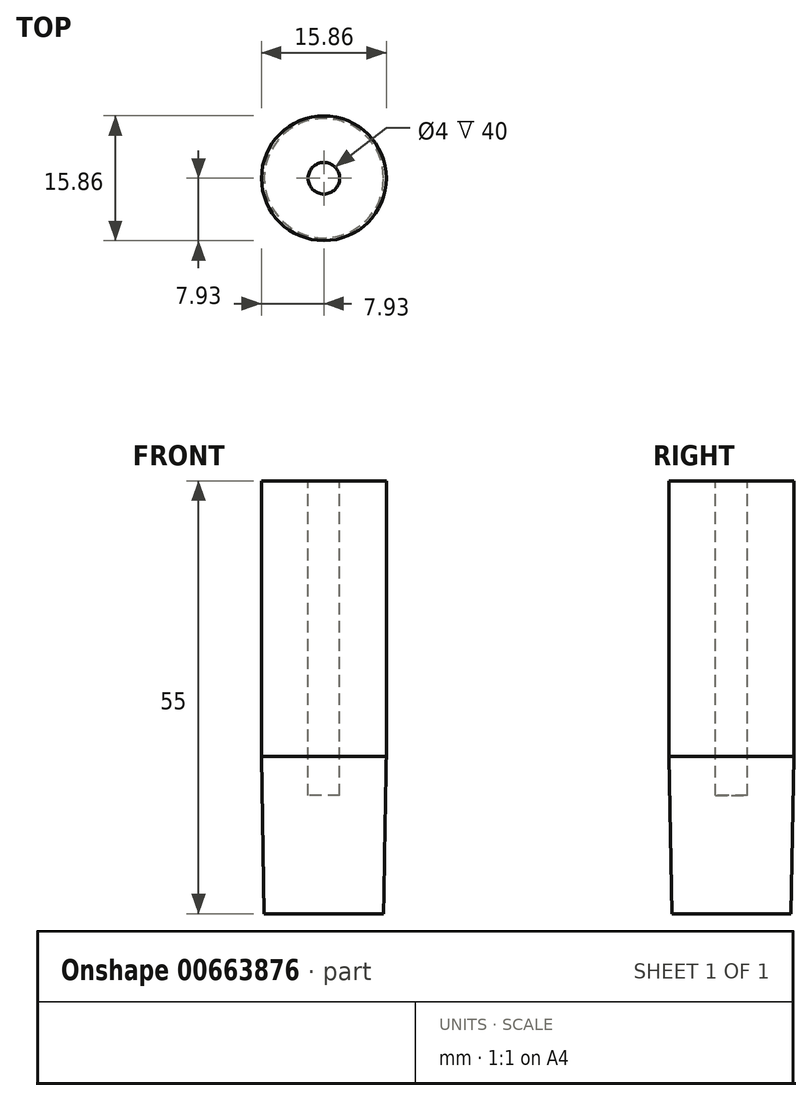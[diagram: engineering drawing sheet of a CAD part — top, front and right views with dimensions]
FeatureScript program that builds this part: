
annotation { "Feature Type Name" : "Feature", "Feature Type Description" : "" }
export const myFeature = defineFeature(function(context is Context, id is Id, definition is map)
    precondition{}
    {
        {
            var Q0;
            Q0=qCreatedBy(makeId("Top.planeOp"),FACE);
            var sketch = newSketch(context, id + "F0", { "sketchPlane" : qUnion([Q0])});
            skCircle(sketch, "E0", {"center": v(0, 0) * mm, "radius": 7.92 * mm});
            skSolve(sketch);
        }
        {
            var Q0;
            Q0 = qSketchRegion(id + "F0", true);
            extrude(context, id + "F1", {"entities" : qUnion([Q0]), "depth" : 55 * mm, "offsetDistance" : 25 * mm});
        }
        {
            var Q0;
            Q0=makeQuery(id+"F1.opExtrude","CAP_FACE",FACE,{"disambiguationData":[OSD([sQuery(id+"F0.wireOp",EDGE,"E0")])],"isStart":false});
            var sketch = newSketch(context, id + "F2", { "sketchPlane" : qUnion([Q0])});
            skCircle(sketch, "E1", {"center": v(0, 0) * mm, "radius": 2 * mm});
            skSolve(sketch);
        }
        {
            var Q0;
            Q0=makeQuery(id+"F1.opExtrude","CAP_EDGE",EDGE,{"disambiguationData":[OSD([sQuery(id+"F0.wireOp",EDGE,"E0")])],"isStart":true});
            chamfer(context, id + "F3", {"entities" : qUnion([Q0]), "chamferType" : ChamferType.OFFSET_ANGLE, "width" : 20 * mm, "oppositeDirection" : false, "angle" : 1 * degree, "tangentPropagation" : true});
        }
        {
            var Q0;
            Q0=makeQuery(id+"F2.imprint","IMPRINT",FACE,{"disambiguationData":[TD([[makeQuery(id+"F2.imprint","IMPRINT",EDGE,{"derivedFrom":sQuery(id+"F2.wireOp",EDGE,"E1")}),1.0]])]});
            extrude(context, id + "F4", {"entities" : qUnion([Q0]), "operationType" : NewBodyOperationType.REMOVE, "oppositeDirection" : true, "depth" : 40 * mm, "offsetDistance" : 25 * mm});
        }
    });
